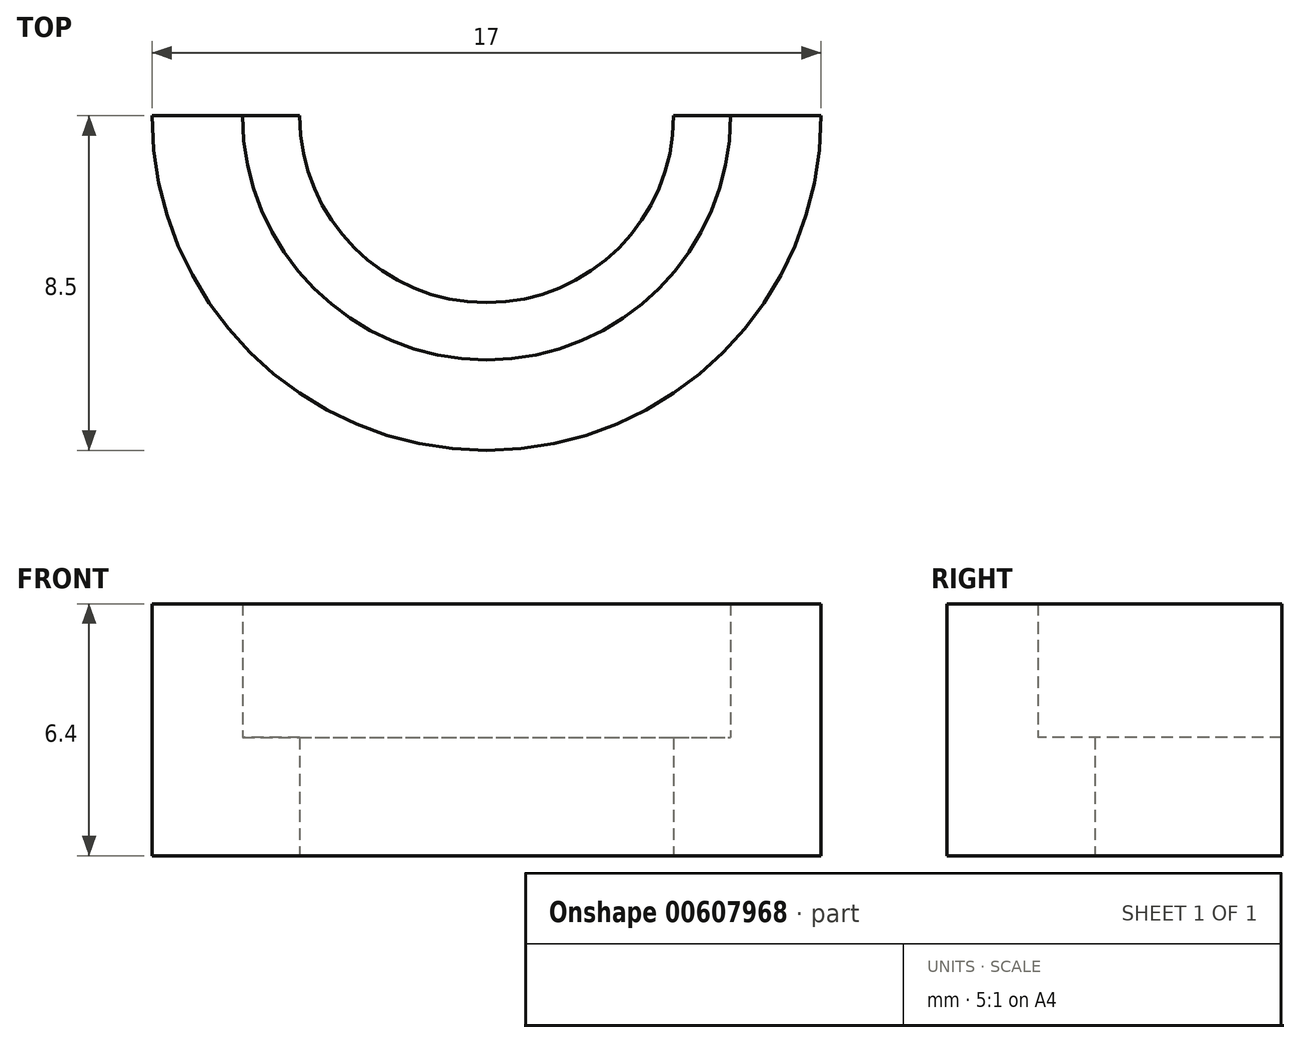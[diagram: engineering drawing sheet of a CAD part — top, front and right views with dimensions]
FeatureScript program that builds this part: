
annotation { "Feature Type Name" : "Feature", "Feature Type Description" : "" }
export const myFeature = defineFeature(function(context is Context, id is Id, definition is map)
    precondition{}
    {
        {
            var Q0;
            Q0=qCreatedBy(makeId("Top.planeOp"),FACE);
            var sketch = newSketch(context, id + "F0", { "sketchPlane" : qUnion([Q0])});
            skCircle(sketch, "E0", {"center": v(0, 0) * mm, "radius": 4.75 * mm, "construction": true});
            skArc(sketch, "E1", {"start": v(-4.75, 0) * mm, "mid": v(0, -4.75) * mm, "end": v(4.75, 0) * mm});
            skLineSegment(sketch, "E2", {"start": v(-4.75, 0) * mm, "end": v(-8.5, 0) * mm});
            skLineSegment(sketch, "E3", {"start": v(4.75, 0) * mm, "end": v(8.5, 0) * mm});
            skArc(sketch, "E4", {"start": v(-8.5, 0) * mm, "mid": v(0, -8.5) * mm, "end": v(8.5, 0) * mm});
            skSolve(sketch);
        }
        {
            var Q0;
            Q0=makeQuery(id+"F0.imprint","IMPRINT",FACE,{"disambiguationData":[TD([[makeQuery(id+"F0.imprint","IMPRINT",EDGE,{"derivedFrom":sQuery(id+"F0.wireOp",EDGE,"E1")}),-1.0]])]});
            extrude(context, id + "F1", {"entities" : qUnion([Q0]), "depth" : 3 * mm, "offsetDistance" : 25 * mm});
        }
        {
            var Q0;
            Q0=makeQuery(id+"F1.opExtrude","CAP_FACE",FACE,{"disambiguationData":[OSD([sQuery(id+"F0.wireOp",EDGE,"E1"),sQuery(id+"F0.wireOp",EDGE,"E2"),sQuery(id+"F0.wireOp",EDGE,"E3"),sQuery(id+"F0.wireOp",EDGE,"E4")])],"isStart":false});
            var sketch = newSketch(context, id + "F2", { "sketchPlane" : qUnion([Q0])});
            skArc(sketch, "E5", {"start": v(-8.5, 0) * mm, "mid": v(0, -8.5) * mm, "end": v(8.5, 0) * mm});
            skArc(sketch, "E6", {"start": v(-6.2, 0) * mm, "mid": v(0, -6.2) * mm, "end": v(6.2, 0) * mm});
            skLineSegment(sketch, "E7", {"start": v(-6.2, 0) * mm, "end": v(-8.5, 0) * mm});
            skLineSegment(sketch, "E8", {"start": v(6.2, 0) * mm, "end": v(8.5, 0) * mm});
            skSolve(sketch);
        }
        {
            var Q0;
            Q0 = qSketchRegion(id + "F2", true);
            extrude(context, id + "F3", {"entities" : qUnion([Q0]), "operationType" : NewBodyOperationType.ADD, "depth" : 3.4 * mm, "offsetDistance" : 25 * mm});
        }
    });
